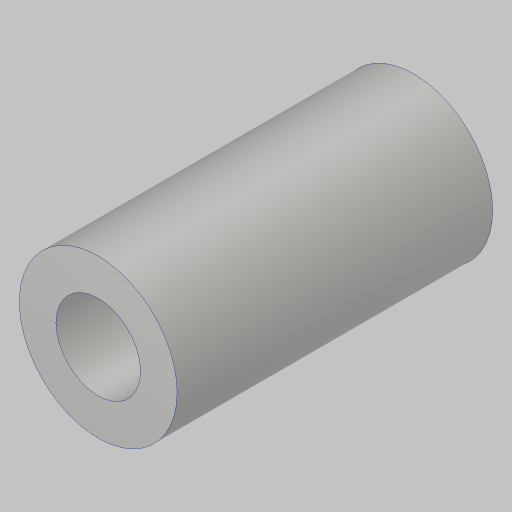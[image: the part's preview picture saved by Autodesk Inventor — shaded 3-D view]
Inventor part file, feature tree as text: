
AUTODESK INVENTOR PART (.ipt)
format: ipt  version: 2023.5 (Build 275446000, 446)  size: 225,792 bytes
history: native  units: in
note: dims shown in document units (in); Inventor stores cm internally (conversion verified against a paired STEP export)
features: extrude x1, hole x1
ambient origin geometry x8: Origin, YZ Plane, XZ Plane, XY Plane, X Axis, Y Axis, Z Axis, Center Point
bodies: Solid1 (feature_tree)
feature tree (2):
  extrude  "Extrusion1"  Depth=0.75in
  hole  "Hole1"  [1 undecoded]
note: 1 required parameter value undecoded (feature->parameter linkage not recoverable at this tier; creation-order binding heuristic only, values carry confidence <= 0.55)
